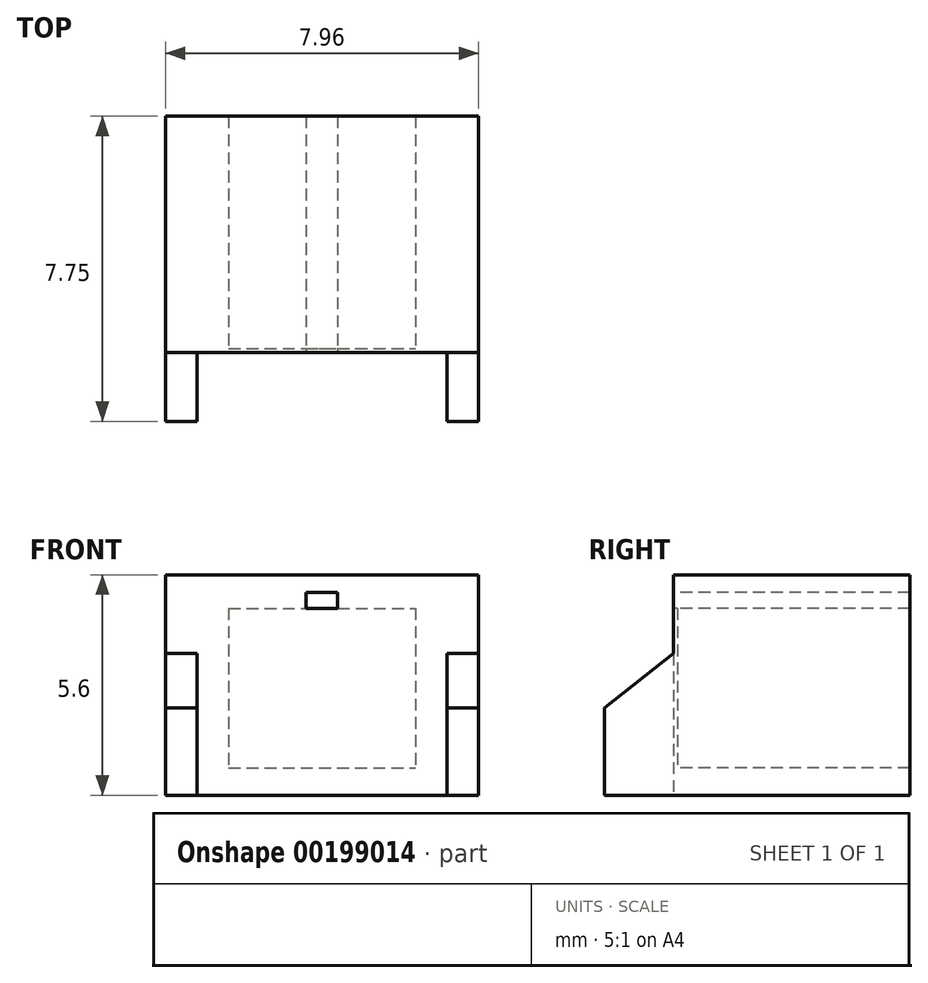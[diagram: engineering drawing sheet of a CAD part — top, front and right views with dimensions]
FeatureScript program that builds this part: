
annotation { "Feature Type Name" : "Feature", "Feature Type Description" : "" }
export const myFeature = defineFeature(function(context is Context, id is Id, definition is map)
    precondition{}
    {
        {
            var Q0;
            Q0=qCreatedBy(makeId("Front.planeOp"),FACE);
            var sketch = newSketch(context, id + "F0", { "sketchPlane" : qUnion([Q0])});
            skLineSegment(sketch, "E0.bottom", {"start": v(-3.97, 2.8) * mm, "end": v(3.98, 2.8) * mm});
            skLineSegment(sketch, "E0.top", {"start": v(-3.98, -2.8) * mm, "end": v(3.97, -2.8) * mm});
            skLineSegment(sketch, "E0.left", {"start": v(-3.98, 2.8) * mm, "end": v(-3.98, -2.8) * mm});
            skLineSegment(sketch, "E0.right", {"start": v(3.98, 2.8) * mm, "end": v(3.97, -2.8) * mm});
            skPoint(sketch, "E0.middle", {"position": v(0, 0) * mm});
            skLineSegment(sketch, "E1", {"start": v(-2.38, 2.8) * mm, "end": v(-2.38, 1.95) * mm});
            skLineSegment(sketch, "E2", {"start": v(-3.98, 1.95) * mm, "end": v(-2.38, 1.95) * mm});
            skLineSegment(sketch, "E3", {"start": v(2.37, -2.8) * mm, "end": v(2.37, -2.1) * mm});
            skLineSegment(sketch, "E4", {"start": v(3.97, -2.1) * mm, "end": v(2.37, -2.1) * mm});
            skLineSegment(sketch, "E5.bottom", {"start": v(-2.38, 1.95) * mm, "end": v(2.37, 1.95) * mm});
            skLineSegment(sketch, "E5.top", {"start": v(-2.38, -2.1) * mm, "end": v(2.37, -2.1) * mm});
            skLineSegment(sketch, "E5.left", {"start": v(-2.38, 1.95) * mm, "end": v(-2.38, -2.1) * mm});
            skLineSegment(sketch, "E5.right", {"start": v(2.37, 1.95) * mm, "end": v(2.37, -2.1) * mm});
            skLineSegment(sketch, "E6.bottom", {"start": v(0, 1.95) * mm, "end": v(0.4, 1.95) * mm});
            skLineSegment(sketch, "E6.top", {"start": v(0, 2.35) * mm, "end": v(0.4, 2.35) * mm});
            skLineSegment(sketch, "E6.left", {"start": v(0, 1.95) * mm, "end": v(0, 2.35) * mm});
            skLineSegment(sketch, "E6.right", {"start": v(0.4, 1.95) * mm, "end": v(0.4, 2.35) * mm});
            skLineSegment(sketch, "E7.bottom", {"start": v(0, 1.95) * mm, "end": v(-0.4, 1.95) * mm});
            skLineSegment(sketch, "E7.top", {"start": v(0, 2.35) * mm, "end": v(-0.4, 2.35) * mm});
            skLineSegment(sketch, "E7.right", {"start": v(-0.4, 1.95) * mm, "end": v(-0.4, 2.35) * mm});
            skSolve(sketch);
        }
        {
            var Q0;
            {var subQ1=sQuery(id+"F0.wireOp",EDGE,"E2");Q0=makeQuery(id+"F0.imprint","IMPRINT",FACE,{"disambiguationData":[TD([[makeQuery(id+"F0.imprint","IMPRINT",EDGE,{"derivedFrom":subQ1}),-1.0]])]});}
            var Q1;
            {var subQ3=sQuery(id+"F0.wireOp",EDGE,"E1");Q1=makeQuery(id+"F0.imprint","IMPRINT",FACE,{"disambiguationData":[TD([[makeQuery(id+"F0.imprint","IMPRINT",EDGE,{"derivedFrom":subQ3}),-1.0]])]});}
            var Q2;
            {var subQ1=sQuery(id+"F0.wireOp",EDGE,"E1");Q2=makeQuery(id+"F0.imprint","IMPRINT",FACE,{"disambiguationData":[TD([[makeQuery(id+"F0.imprint","IMPRINT",EDGE,{"derivedFrom":subQ1}),1.0]])]});}
            var Q3;
            {var subQ3=sQuery(id+"F0.wireOp",EDGE,"E3");Q3=makeQuery(id+"F0.imprint","IMPRINT",FACE,{"disambiguationData":[TD([[makeQuery(id+"F0.imprint","IMPRINT",EDGE,{"derivedFrom":subQ3}),-1.0]])]});}
            extrude(context, id + "F1", {"entities" : qUnion([Q0, Q1, Q2, Q3]), "oppositeDirection" : true, "depth" : 6 * mm});
        }
        {
            var Q0;
            Q0=makeQuery(id+"F0.imprint","IMPRINT",FACE,{"disambiguationData":[TD([[makeQuery(id+"F0.imprint","IMPRINT",EDGE,{"derivedFrom":sQuery(id+"F0.wireOp",EDGE,"E5.bottom")}),-1.0]])]});
            var Q1;
            Q1=makeQuery(id+"F0.imprint","IMPRINT",FACE,{"disambiguationData":[TD([[makeQuery(id+"F0.imprint","IMPRINT",EDGE,{"derivedFrom":sQuery(id+"F0.wireOp",EDGE,"E7.bottom")}),-1.0]])]});
            var Q2;
            Q2=makeQuery(id+"F0.imprint","IMPRINT",FACE,{"disambiguationData":[TD([[makeQuery(id+"F0.imprint","IMPRINT",EDGE,{"derivedFrom":sQuery(id+"F0.wireOp",EDGE,"E6.bottom")}),1.0]])]});
            extrude(context, id + "F2", {"entities" : qUnion([Q0, Q1, Q2]), "operationType" : NewBodyOperationType.ADD, "oppositeDirection" : true, "depth" : 0.1 * mm});
        }
        {
            var Q0;
            Q0=makeQuery(id+"F1.opExtrude","SWEPT_FACE",FACE,{"disambiguationData":[OSD([sQuery(id+"F0.wireOp",EDGE,"E0.right")])]});
            var sketch = newSketch(context, id + "F3", { "sketchPlane" : qUnion([Q0])});
            skLineSegment(sketch, "E8", {"start": v(0, 2.8) * mm, "end": v(0, 0.8) * mm});
            skLineSegment(sketch, "E9", {"start": v(0, 0.8) * mm, "end": v(-1.75, -0.58) * mm});
            skLineSegment(sketch, "E10", {"start": v(-1.75, -0.58) * mm, "end": v(-1.75, -2.8) * mm});
            skLineSegment(sketch, "E11", {"start": v(-1.75, -2.8) * mm, "end": v(0, -2.8) * mm});
            skLineSegment(sketch, "E12", {"start": v(0, -2.8) * mm, "end": v(0, 0.8) * mm});
            skSolve(sketch);
        }
        {
            var Q0;
            Q0=makeQuery(id+"F3.imprint","IMPRINT",FACE,{"disambiguationData":[TD([[makeQuery(id+"F3.imprint","IMPRINT",EDGE,{"derivedFrom":sQuery(id+"F3.wireOp",EDGE,"E9")}),1.0]])]});
            extrude(context, id + "F4", {"entities" : qUnion([Q0]), "operationType" : NewBodyOperationType.ADD, "oppositeDirection" : true, "depth" : 0.8 * mm});
        }
        {
            var Q0;
            Q0=makeQuery(id+"F1.opExtrude","SWEPT_FACE",FACE,{"disambiguationData":[OSD([sQuery(id+"F0.wireOp",EDGE,"E0.left")])]});
            var sketch = newSketch(context, id + "F5", { "sketchPlane" : qUnion([Q0])});
            skLineSegment(sketch, "E13", {"start": v(0, 2.8) * mm, "end": v(0, 0.8) * mm});
            skLineSegment(sketch, "E14", {"start": v(0, 0.8) * mm, "end": v(1.75, -0.58) * mm});
            skLineSegment(sketch, "E15", {"start": v(1.75, -0.58) * mm, "end": v(1.75, -2.8) * mm});
            skLineSegment(sketch, "E16", {"start": v(1.75, -2.8) * mm, "end": v(0, -2.8) * mm});
            skSolve(sketch);
        }
        {
            var Q0;
            {var subQ0=sQuery(id+"F5.wireOp",EDGE,"E14");Q0=makeQuery(id+"F5.imprint","IMPRINT",FACE,{"disambiguationData":[TD([[makeQuery(id+"F5.imprint","IMPRINT",EDGE,{"derivedFrom":subQ0}),-1.0]])]});}
            extrude(context, id + "F6", {"entities" : qUnion([Q0]), "operationType" : NewBodyOperationType.ADD, "oppositeDirection" : true, "depth" : 0.8 * mm});
        }
    });
